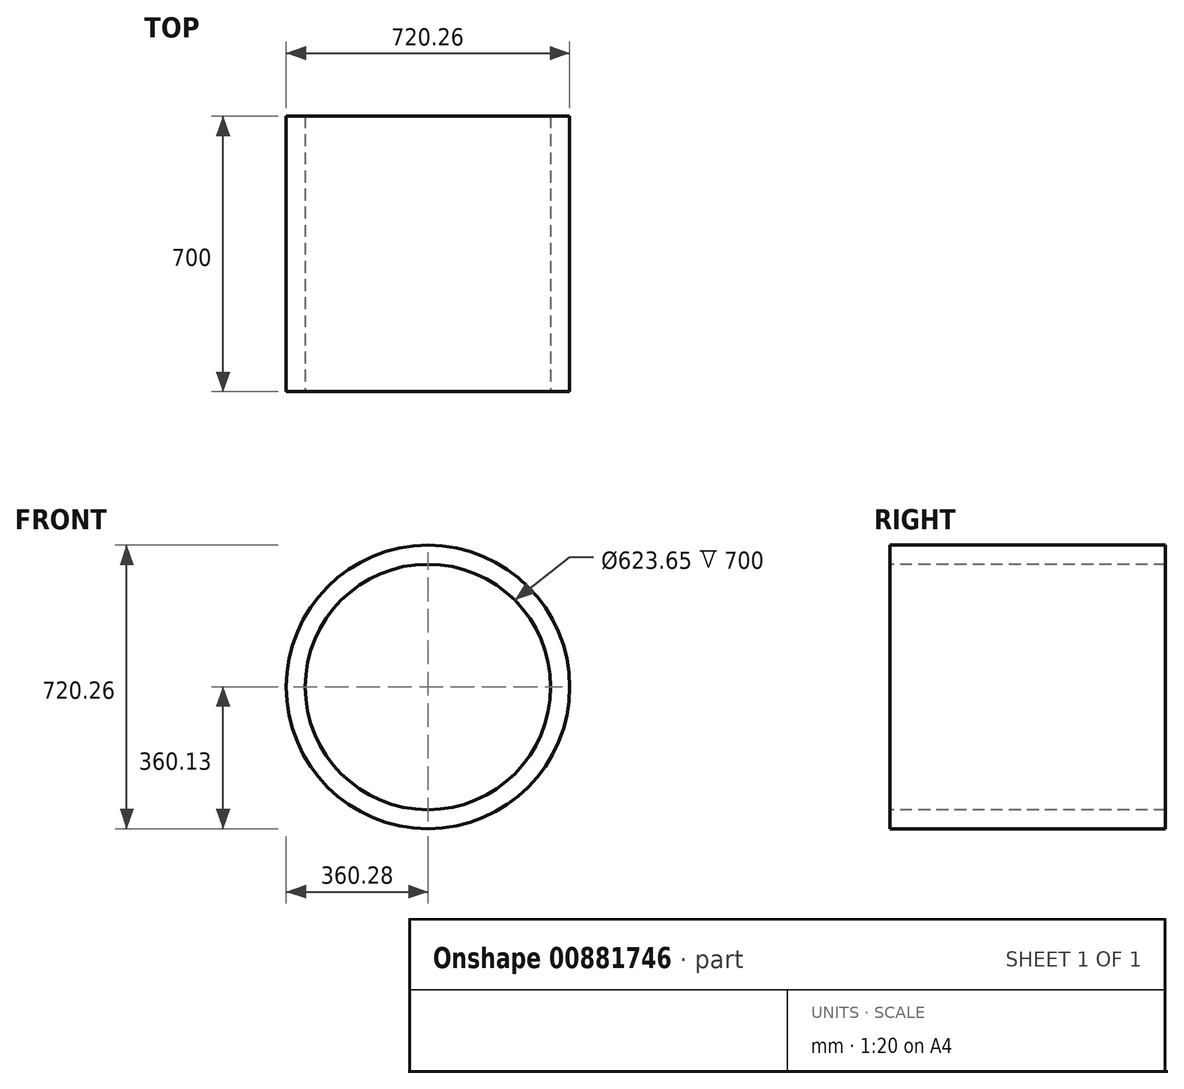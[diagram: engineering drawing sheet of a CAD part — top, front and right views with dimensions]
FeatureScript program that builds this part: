
annotation { "Feature Type Name" : "Feature", "Feature Type Description" : "" }
export const myFeature = defineFeature(function(context is Context, id is Id, definition is map)
    precondition{}
    {
        {
            var Q0;
            Q0=qCreatedBy(makeId("Front.planeOp"),FACE);
            var sketch = newSketch(context, id + "F0", { "sketchPlane" : qUnion([Q0])});
            skCircle(sketch, "E0", {"center": v(0, 0) * mm, "radius": 0.15 * mm});
            skCircle(sketch, "E1", {"center": v(0.15, 0) * mm, "radius": 0.15 * mm});
            skCircle(sketch, "E2", {"center": v(0.3, 0) * mm, "radius": 0.15 * mm});
            skCircle(sketch, "E3", {"center": v(0.45, 0) * mm, "radius": 0.15 * mm});
            skSolve(sketch);
        }
        {
            var Q0;
            Q0=qCreatedBy(makeId("Right.planeOp"),FACE);
            cPlane(context, id + "F1", {"entities" : qUnion([Q0]), "cplaneType" : CPlaneType.OFFSET, "offset" : 0.15 * mm, "width" : 150 * mm, "height" : 150 * mm});
        }
        {
            var Q0;
            Q0=qCreatedBy(id+"F1.planeOp",FACE);
            cPlane(context, id + "F2", {"entities" : qUnion([Q0]), "cplaneType" : CPlaneType.OFFSET, "offset" : .15 * mm, "width" : 150 * mm, "height" : 150 * mm});
        }
        {
            var Q0;
            Q0=qCreatedBy(makeId("Front.planeOp"),FACE);
            var sketch = newSketch(context, id + "F3", { "sketchPlane" : qUnion([Q0])});
            skCircle(sketch, "E4", {"center": v(0, 0) * mm, "radius": 360.12 * mm});
            skSolve(sketch);
        }
        {
            var Q0;
            Q0=makeQuery(id+"F3.imprint","IMPRINT",FACE,{"disambiguationData":[TD([[makeQuery(id+"F3.imprint","IMPRINT",EDGE,{"derivedFrom":sQuery(id+"F3.wireOp",EDGE,"E4")}),1.0]])]});
            extrude(context, id + "F4", {"entities" : qUnion([Q0]), "oppositeDirection" : true, "depth" : 700 * mm, "offsetDistance" : 25 * mm});
        }
        {
            var Q0;
            Q0=qCreatedBy(makeId("Front.planeOp"),FACE);
            var sketch = newSketch(context, id + "F5", { "sketchPlane" : qUnion([Q0])});
            skCircle(sketch, "E5", {"center": v(0.15, 0) * mm, "radius": 311.83 * mm});
            skSolve(sketch);
        }
        {
            var Q0;
            Q0=makeQuery(id+"F5.imprint","IMPRINT",FACE,{"disambiguationData":[TD([[makeQuery(id+"F5.imprint","IMPRINT",EDGE,{"derivedFrom":sQuery(id+"F5.wireOp",EDGE,"E5")}),1.0]])]});
            extrude(context, id + "F6", {"entities" : qUnion([Q0]), "operationType" : NewBodyOperationType.REMOVE, "oppositeDirection" : true, "depth" : 700 * mm, "offsetDistance" : 25 * mm});
        }
    });
